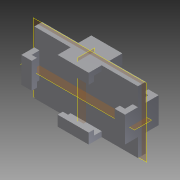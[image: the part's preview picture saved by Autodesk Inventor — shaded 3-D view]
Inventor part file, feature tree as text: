
AUTODESK INVENTOR PART (.ipt)
format: ipt  version: 2012 SP1 (Build 160190100, 190)  size: 161,792 bytes
history: native  units: in
note: dims shown in document units (in); Inventor stores cm internally (conversion verified against a paired STEP export)
features: extrude x5, sketch x5, plane x3, mirror x3
ambient origin geometry x8: Origin, YZ Plane, XZ Plane, XY Plane, X Axis, Y Axis, Z Axis, Center Point
bodies: Solid1 (feature_tree)
feature tree (16):
  extrude  "Extrusion1"  Depth=3.0in
  extrude  "Extrusion2"  Depth=1.5in
  plane  "Work Plane1"
  plane  "Work Plane2"
  extrude  "Extrusion3"  Depth=0.375in TaperAngle=0.0deg
  extrude  "Extrusion4"  Depth=0.25in
  extrude  "Extrusion5"  Depth=1.5in
  mirror  "Mirror3"
  mirror  "Mirror4"
  plane  "Work Plane3"
  mirror  "Mirror5"
  sketch  "Sketch1"  dims[d0=5.0in d1=3.0in]
  sketch  "Sketch2"  dims[d2=0.375in d3=0.0in d4=1.5in]
  sketch  "Sketch3"  dims[d5=0.25in d6=0.375in d7=0.0in]
  sketch  "Sketch4"  dims[d8=1.25in d9=0.25in]
  sketch  "Sketch5"  dims[d10=0.375in d11=0.0in d12=1.5in d13=1.5in d14=0.5in d15=0.25in d16=0.0in d17=1.25in d18=1.25in d19=0.5in d20=0.25in d21=0.0in]
